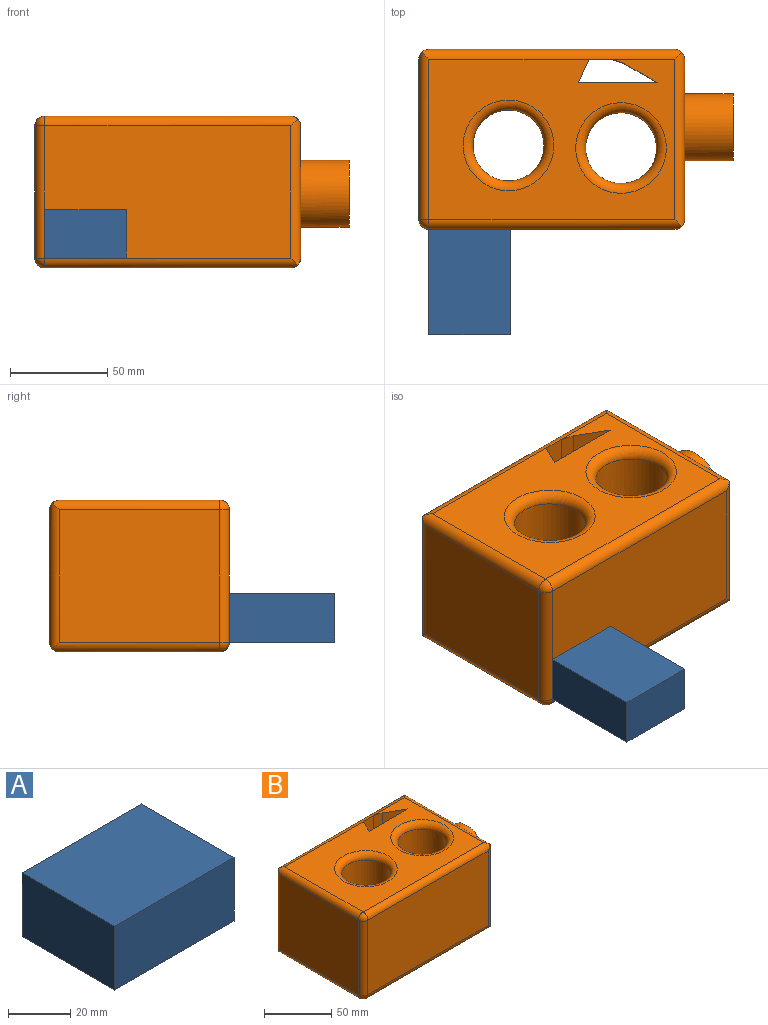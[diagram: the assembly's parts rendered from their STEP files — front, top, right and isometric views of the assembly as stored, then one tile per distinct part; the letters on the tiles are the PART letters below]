
ASSEMBLY  parts=2 mates=1
PART A: 6 faces, bbox 54.2x42x25 mm
  f0: plane 54.16x25mm, normal (0,-1,0), area 1353.9mm2, adj f1,f3,f4,f5
  f1: plane 42.05x25mm, normal (1,0,0), area 1051.2mm2, adj f0,f2,f4,f5
  f2: plane 54.16x25mm, normal (0,1,0), area 1353.9mm2, adj f1,f3,f4,f5
  f3: plane 42.05x25mm, normal (-1,0,0), area 1051.2mm2, adj f0,f2,f4,f5
  f4: plane 54.16x42.05mm, normal (0,0,1), area 2277.2mm2, adj f0,f1,f2,f3
  f5: plane 54.16x42.05mm, normal (0,0,-1), area 2277.2mm2, adj f0,f1,f2,f3
PART B: 43 faces, bbox 161.9x92.7x78.2 mm
  f0: plane 68.07x51.96mm, normal (0,1,0), area 3004.5mm2, adj f10,f18,f20,f27
  f1: plane 68.07x43.79mm, normal (0,1,0), area 2981.1mm2, adj f18,f19,f20,f29
  f2: plane 82.54x68.07mm, normal (-1,0,0), area 5618.8mm2, adj f10,f11,f14,f17
  f3: plane 126.75x68.07mm, normal (0,-1,0), area 8627.9mm2, adj f9,f12,f13,f17
  f4: plane 82.54x68.07mm, normal (1,0,0), area 4682.9mm2, adj f9,f19,f21,f22,f37
  f5: cylinder r=18.29mm len=68.07mm, axis (0,0,-1), area 7823mm2, adj f24,f26
  f6: cylinder r=18.25mm len=68.07mm, axis (0,0,-1), area 7513.8mm2, adj f23,f25,f39,f40,f41,f42
  f7: plane 126.75x82.54mm, normal (0,0,1), area 6705.5mm2, adj f11,f12,f20,f21,f23,f24,f32,f33
  f8: plane 126.75x82.54mm, normal (0,0,-1), area 6705.5mm2, adj f13,f14,f18,f22,f25,f26,f32,f33
  f9: cylinder r=5.08mm len=75.26mm, axis (0,0,-1), area 573.4mm2, adj f3,f4,f12,f13,f21,f22
  f10: cylinder r=5.08mm len=75.26mm, axis (0,0,-1), area 573.4mm2, adj f0,f2,f11,f14,f18,f20
  f11: cylinder r=5.08mm len=86.14mm, axis (0,1,0), area 673.8mm2, adj f2,f7,f10,f15,f20
  f12: cylinder r=5.08mm len=130.34mm, axis (-1,0,0), area 1026.5mm2, adj f3,f7,f9,f15,f21
  f13: cylinder r=5.08mm len=130.34mm, axis (1,0,0), area 1026.5mm2, adj f3,f8,f9,f16,f22
  f14: cylinder r=5.08mm len=86.14mm, axis (0,-1,0), area 673.8mm2, adj f2,f8,f10,f16,f18
  f15: sphere r=5.08mm, area 40.5mm2, adj f11,f12,f17
  f16: sphere r=5.08mm, area 40.5mm2, adj f13,f14,f17
  f17: cylinder r=5.08mm len=68.07mm, axis (0,0,1), area 543.2mm2, adj f2,f3,f15,f16
  f18: cylinder r=5.08mm len=133.93mm, axis (-1,0,0), area 1041.6mm2, adj f0,f1,f8,f10,f14,f19,f22,f30
  f19: cylinder r=5.08mm len=75.26mm, axis (0,0,1), area 573.4mm2, adj f1,f4,f18,f20,f21,f22
  f20: cylinder r=5.08mm len=133.93mm, axis (1,0,0), area 1041.6mm2, adj f0,f1,f7,f10,f11,f19,f21,f28
  f21: cylinder r=5.08mm len=89.73mm, axis (0,-1,0), area 688.9mm2, adj f4,f7,f9,f12,f19,f20
  f22: cylinder r=5.08mm len=89.73mm, axis (0,1,0), area 688.9mm2, adj f4,f8,f9,f13,f18,f19
  f23: torus R=23.33mm, axis (0,0,1), area 1007.7mm2, adj f6,f7
  f24: torus R=23.37mm, axis (0,0,1), area 1009.6mm2, adj f5,f7
  f25: torus R=23.33mm, axis (0,0,1), area 1007.7mm2, adj f6,f8
  f26: torus R=23.37mm, axis (0,0,1), area 1009.6mm2, adj f5,f8
  f27: plane 68.07x15.65mm, normal (0.97,0,0.22), area 873.1mm2, adj f0,f28,f30,f31
  f28: plane 46.64x12.5mm, normal (0,0,-1), area 568mm2, adj f20,f27,f29,f31,f35,f36
  f29: plane 68.07x5.08mm, normal (-1,0,0), area 345.8mm2, adj f1,f28,f30,f35
  f30: plane 30.99x12.5mm, normal (0,0,1), area 372.4mm2, adj f18,f27,f29,f31,f35,f36
  f31: plane 68.07x42.89mm, normal (0,1,0), area 2386.9mm2, adj f27,f28,f30,f36
  f32: plane 78.23x40.82mm, normal (0,1,0), area 3193.7mm2, adj f7,f8,f33,f36
  f33: plane 78.23x17.36mm, normal (-0.5,-0.87,0), area 1568mm2, adj f7,f8,f32,f34
  f34: plane 78.23x6.57mm, normal (-0.31,-0.95,0), area 539.9mm2, adj f7,f8,f33,f35
  f35: plane 78.23x11.24mm, normal (0,-1,0), area 859.3mm2, adj f18,f20,f28,f29,f30,f34,f36
  f36: plane 78.23x12.13mm, normal (0.91,-0.42,0), area 490.1mm2, adj f7,f8,f28,f30,f31,f32,f35
  f37: cylinder r=17.26mm len=34.52mm, axis (-1,0,0), area 2711.2mm2, adj f4,f38
  f38: plane 34.52x34.52mm, normal (1,0,0), area 740.3mm2, adj f37,f39,f40,f41,f42
  f39: plane 53.14x12.65mm, normal (0,0,-1), area 561.1mm2, adj f6,f38,f40,f41
  f40: plane 40.19x15.46mm, normal (0,1,0), area 621.3mm2, adj f6,f38,f39,f42
  f41: plane 53.14x15.46mm, normal (0,-1,0), area 821.4mm2, adj f6,f38,f39,f42
  f42: plane 53.14x12.65mm, normal (0,0,1), area 561.1mm2, adj f6,f38,f40,f41
PLACE A rot(axis=(0,0,-1),90deg) t=(5.08,-54.16,5.08)mm
PLACE B at identity fixed
MATE slider B.f14 <-> A.f3  axis (0,-1,0) through (5.08,0,5.08)mm
